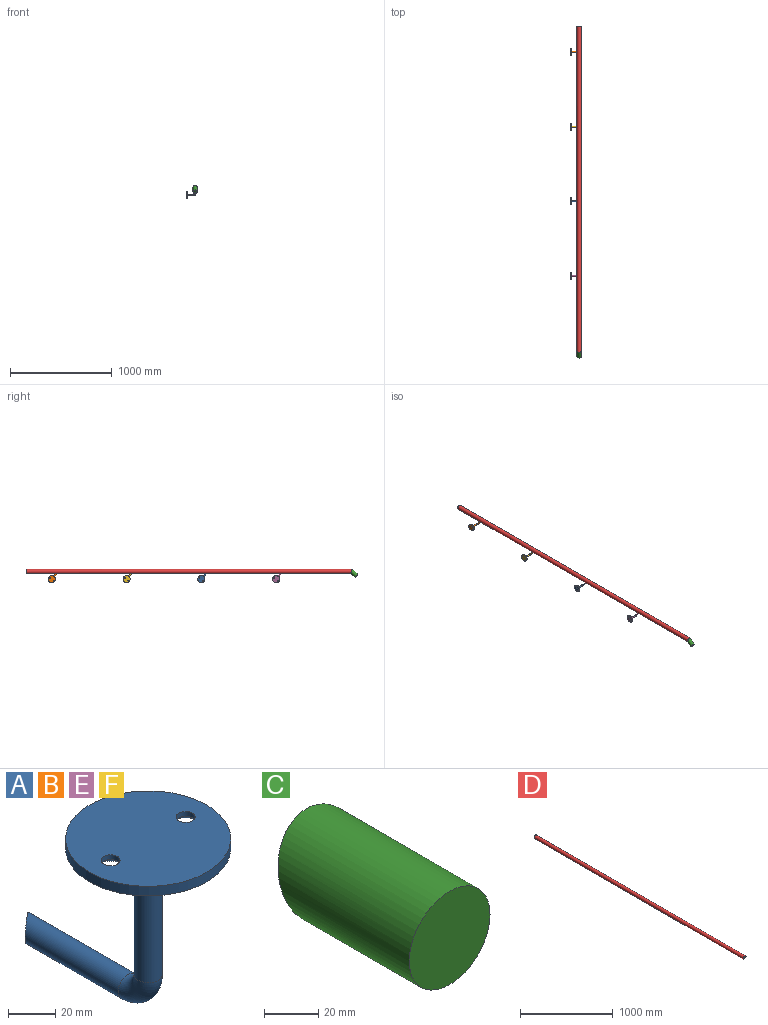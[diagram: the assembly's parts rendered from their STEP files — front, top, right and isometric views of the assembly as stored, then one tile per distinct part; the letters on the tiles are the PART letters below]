
ASSEMBLY  parts=6 mates=5
PART A: 11 faces, bbox 72.1x114.6x92.1 mm
  f0: cylinder r=6mm len=65.53mm, axis (0,-1,0), area 2289.2mm2, adj f1,f10
  f1: torus R=12mm, axis (-1,0,0), area 710.6mm2, adj f0,f2
  f2: cylinder r=6mm len=65.5mm, axis (0,0,1), area 2469.3mm2, adj f1,f5
  f3: cylinder r=35mm len=70mm, axis (0,0,-1), area 1099.6mm2, adj f4,f5
  f4: plane 70x70mm, normal (0,0,1), area 3747.9mm2, adj f3,f6,f7
  f5: plane 70x70mm, normal (0,0,-1), area 3469.9mm2, adj f2,f3,f8,f9
  f6: cylinder r=4mm len=8mm, axis (0,0,-1), area 62.8mm2, adj f4,f9
  f7: cylinder r=4mm len=8mm, axis (0,0,-1), area 62.8mm2, adj f4,f8
  f8: cone r=4mm half-angle=45deg, axis (0,0,-1), area 116.6mm2, adj f5,f7
  f9: cone r=4mm half-angle=45deg, axis (0,0,-1), area 116.6mm2, adj f5,f6
  f10: plane 14.08x14.08mm, normal (-0.64,0.77,0), area 146.6mm2, adj f0
PART B: same geometry as A
PART C: 5 faces, bbox 42.3x75x42.3 mm
  f0: cylinder r=18.5mm len=69.05mm, axis (0,1,0), area 7254.1mm2, adj f3,f4
  f1: cylinder r=21.15mm len=75mm, axis (0,1,0), area 8957.6mm2, adj f2,f4
  f2: plane 42.3x42.3mm, normal (0,-1,0), area 1405.3mm2, adj f1
  f3: plane 37x37mm, normal (0,1,0), area 1075.2mm2, adj f0
  f4: plane 42.3x42.3mm, normal (0,0.94,-0.34), area 350.7mm2, adj f0,f1
PART D: 7 faces, bbox 42.4x3200.1x41.5 mm
  f0: plane 3185.09x12mm, normal (0,0,-1), area 38221.1mm2, adj f1,f2,f3
  f1: cylinder r=21.2mm len=3200.09mm, axis (0,1,0), area 386489.3mm2, adj f0,f2,f3
  f2: plane 42.4x41.53mm, normal (0,1,0), area 1405mm2, adj f0,f1
  f3: plane 42.4x41.53mm, normal (0,-0.94,-0.34), area 685.4mm2, adj f0,f1,f4,f5
  f4: plane 32.82x10.68mm, normal (0,1,0), area 252.3mm2, adj f3,f5
  f5: cylinder r=17.95mm len=3190mm, axis (0,1,0), area 359380.4mm2, adj f3,f4,f6
  f6: plane 35.9x35.9mm, normal (0,-1,0), area 1012.2mm2, adj f5
PART E: same geometry as A
PART F: same geometry as A
PLACE A rot(axis=(0.67,-0.32,-0.67),144.9deg) t=(24.09,1679.81,-90.84)mm
PLACE B rot(axis=(0.67,-0.32,-0.67),144.9deg) t=(24.09,3146.47,-90.84)mm
PLACE C rot(axis=(1,0,0),39.5deg) t=(24.09,263.06,-69.4)mm
PLACE D t=(24.09,249.62,-74.32)mm
PLACE E rot(axis=(0.67,-0.32,-0.67),144.9deg) t=(24.09,946.47,-90.84)mm
PLACE F rot(axis=(0.67,-0.32,-0.67),144.9deg) t=(24.09,2413.14,-90.84)mm
MATE fastened F.f10 <-> D.f0  axis (0,0,1) through (24.09,2416.29,-94.65)mm
MATE fastened E.f10 <-> D.f0  axis (0,0,1) through (24.09,949.62,-94.65)mm
MATE fastened B.f10 <-> D.f0  axis (0,0,1) through (24.09,3149.62,-94.65)mm
MATE fastened A.f10 <-> D.f0  axis (0,0,1) through (24.09,1682.96,-94.65)mm
MATE fastened C.f4 <-> D.f3  axis (0,0.94,0.34) through (24.09,257.2,-74.23)mm
